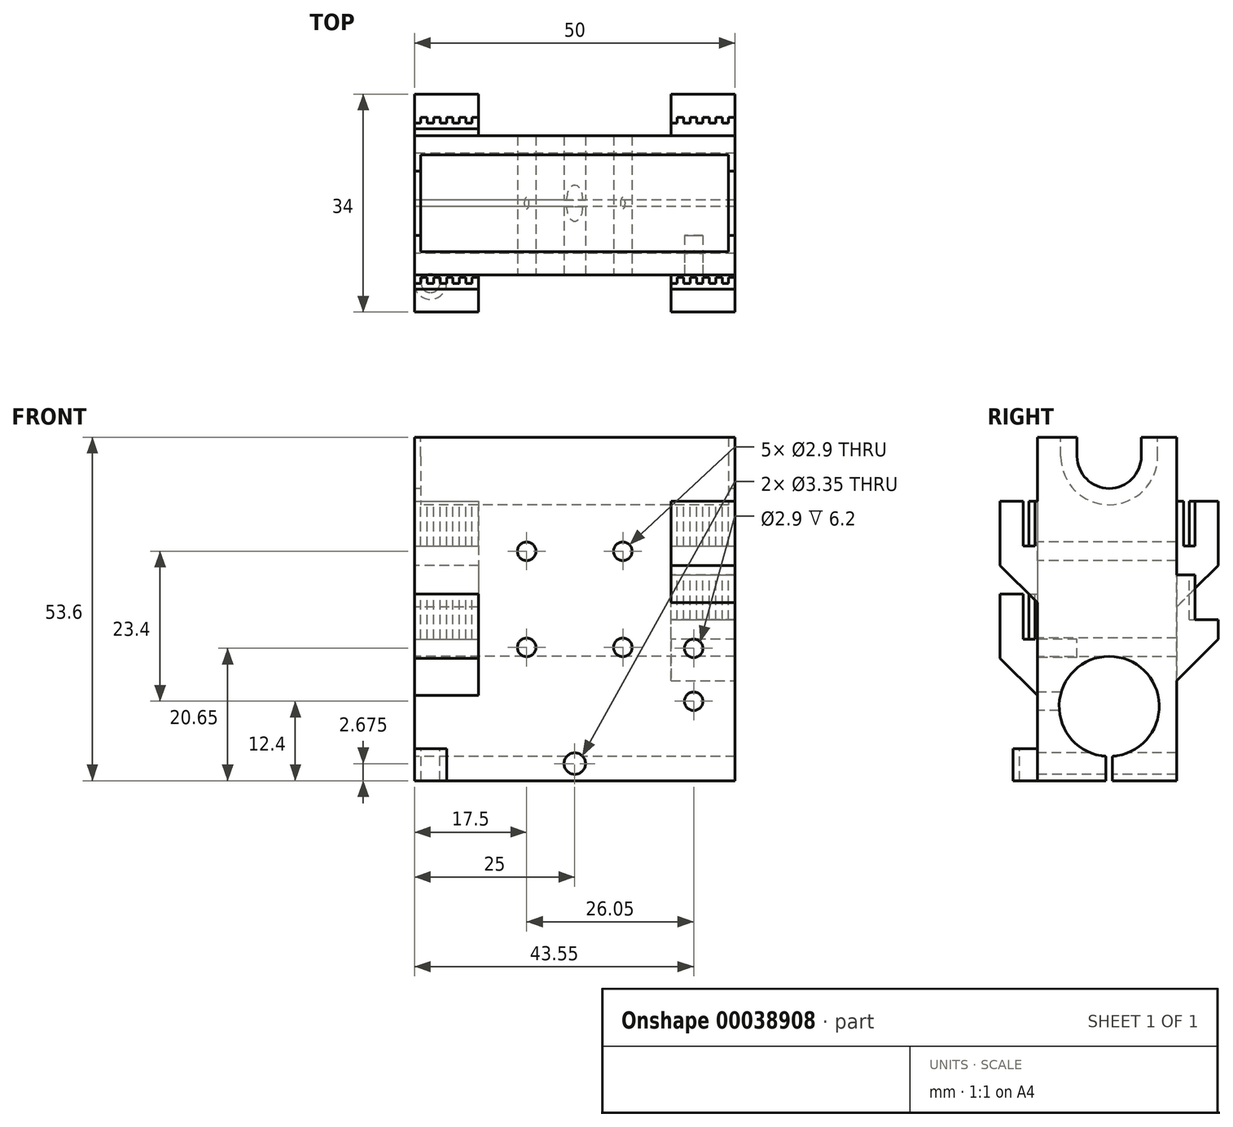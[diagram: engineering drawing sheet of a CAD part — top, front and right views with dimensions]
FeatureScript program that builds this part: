
annotation { "Feature Type Name" : "Feature", "Feature Type Description" : "" }
export const myFeature = defineFeature(function(context is Context, id is Id, definition is map)
    precondition{}
    {
        {
            var Q0;
            Q0=qCreatedBy(makeId("Top.planeOp"),FACE);
            var sketch = newSketch(context, id + "F0", { "sketchPlane" : qUnion([Q0])});
            skLineSegment(sketch, "E0.bottom", {"start": v(0, 0) * mm, "end": v(50, 0) * mm});
            skLineSegment(sketch, "E0.top", {"start": v(0, 20) * mm, "end": v(50, 20) * mm});
            skLineSegment(sketch, "E0.left", {"start": v(0, 0) * mm, "end": v(0, 20) * mm});
            skLineSegment(sketch, "E0.right", {"start": v(50, 0) * mm, "end": v(50, 20) * mm});
            skSolve(sketch);
        }
        {
            var Q0;
            Q0=qSketchRegion(id+"F0",true);
            extrude(context, id + "F1", {"entities" : qUnion([Q0]), "depth" : 50.6 * mm, "hasSecondDirection" : true, "secondDirectionOppositeDirection" : true, "secondDirectionDepth" : 3 * mm});
        }
        {
            var Q0;
            Q0=makeQuery(id+"F1.opExtrude","SWEPT_FACE",FACE,{"disambiguationData":[OSD([sQuery(id+"F0.wireOp",EDGE,"E0.left")])]});
            var sketch = newSketch(context, id + "F2", { "sketchPlane" : qUnion([Q0])});
            skCircle(sketch, "E1", {"center": v(-10, 8.6) * mm, "radius": 7.8 * mm});
            skCircle(sketch, "E2", {"center": v(-10, 47.6) * mm, "radius": 5 * mm});
            skLineSegment(sketch, "E3", {"start": v(-20, 47.6) * mm, "end": v(0, 47.6) * mm, "construction": true});
            skLineSegment(sketch, "E4", {"start": v(-15, 50.6) * mm, "end": v(-15, 47.6) * mm});
            skLineSegment(sketch, "E5", {"start": v(-5, 50.6) * mm, "end": v(-5, 47.6) * mm});
            skLineSegment(sketch, "E6", {"start": v(-20, 8.6) * mm, "end": v(0, 8.6) * mm, "construction": true});
            skLineSegment(sketch, "E7", {"start": v(-10, 8.6) * mm, "end": v(-10, -3) * mm, "construction": true});
            skLineSegment(sketch, "E8", {"start": v(-10, -3) * mm, "end": v(-10.5, -3) * mm});
            skLineSegment(sketch, "E9", {"start": v(-10.5, -3) * mm, "end": v(-10.5, 0.82) * mm});
            skLineSegment(sketch, "E10", {"start": v(-10.5, 0.82) * mm, "end": v(-9.5, 0.82) * mm});
            skLineSegment(sketch, "E11", {"start": v(-9.5, 0.82) * mm, "end": v(-9.5, 0) * mm});
            skLineSegment(sketch, "E12", {"start": v(-9.5, -3) * mm, "end": v(-10, -3) * mm});
            skLineSegment(sketch, "E13", {"start": v(-10, 15.6) * mm, "end": v(-10, 16.4) * mm});
            skLineSegment(sketch, "E14", {"start": v(-10, 15.6) * mm, "end": v(-5.38, 14.88) * mm});
            skLineSegment(sketch, "E15", {"start": v(-10, 15.6) * mm, "end": v(-14.62, 14.88) * mm});
            skCircle(sketch, "E16", {"center": v(-10, 47.6) * mm, "radius": 7.55 * mm});
            skLineSegment(sketch, "E17", {"start": v(-2.45, 47.6) * mm, "end": v(-2.45, 50.6) * mm});
            skLineSegment(sketch, "E18", {"start": v(-17.55, 47.6) * mm, "end": v(-17.55, 50.6) * mm});
            skLineSegment(sketch, "E19", {"start": v(-9.5, -3) * mm, "end": v(-9.5, 0) * mm});
            skSolve(sketch);
        }
        {
            var Q0;
            {var subQ0=sQuery(id+"F2.wireOp",EDGE,"E14");var subQ1=sQuery(id+"F2.wireOp",EDGE,"E1");var subQ3=makeQuery(id+"F2.imprint","INTERSECT",VERTEX,{"disambiguationData":[OD(0.0)],"derivedFrom":[subQ1,subQ0]});Q0=makeQuery(id+"F2.imprint","IMPRINT",FACE,{"disambiguationData":[TD([[makeQuery(id+"F2.imprint","IMPRINT",EDGE,{"disambiguationData":[TD([[subQ3,-1.0]])],"derivedFrom":subQ1}),1.0]])]});}
            var Q1;
            {var subQ0=sQuery(id+"F2.wireOp",EDGE,"E15");var subQ1=sQuery(id+"F2.wireOp",EDGE,"E1");var subQ3=makeQuery(id+"F2.imprint","INTERSECT",VERTEX,{"disambiguationData":[OD(0.0)],"derivedFrom":[subQ1,subQ0]});Q1=makeQuery(id+"F2.imprint","IMPRINT",FACE,{"disambiguationData":[TD([[makeQuery(id+"F2.imprint","IMPRINT",EDGE,{"disambiguationData":[TD([[subQ3,1.0]])],"derivedFrom":subQ1}),1.0]])]});}
            var Q2;
            Q2=makeQuery(id+"F2.imprint","IMPRINT",FACE,{"disambiguationData":[TD([[makeQuery(id+"F2.imprint","IMPRINT",EDGE,{"derivedFrom":sQuery(id+"F2.wireOp",EDGE,"E8")}),-1.0]])]});
            var Q3;
            {var subQ0=sQuery(id+"F2.wireOp",EDGE,"E10");Q3=makeQuery(id+"F2.imprint","IMPRINT",FACE,{"disambiguationData":[TD([[makeQuery(id+"F2.imprint","IMPRINT",EDGE,{"derivedFrom":subQ0}),-1.0]])]});}
            var Q4;
            {var subQ3=sQuery(id+"F2.wireOp",EDGE,"E13");Q4=makeQuery(id+"F2.imprint","IMPRINT",FACE,{"disambiguationData":[TD([[makeQuery(id+"F2.imprint","IMPRINT",EDGE,{"derivedFrom":subQ3}),-1.0]])]});}
            var Q5;
            {var subQ3=sQuery(id+"F2.wireOp",EDGE,"E13");Q5=makeQuery(id+"F2.imprint","IMPRINT",FACE,{"disambiguationData":[TD([[makeQuery(id+"F2.imprint","IMPRINT",EDGE,{"derivedFrom":subQ3}),1.0]])]});}
            var Q6;
            {var subQ7=sQuery(id+"F2.wireOp",EDGE,"E10");Q6=makeQuery(id+"F2.imprint","IMPRINT",FACE,{"disambiguationData":[TD([[makeQuery(id+"F2.imprint","IMPRINT",EDGE,{"derivedFrom":subQ7}),1.0]])]});}
            var Q7;
            {var subQ3=sQuery(id+"F2.wireOp",EDGE,"E5");Q7=makeQuery(id+"F2.imprint","IMPRINT",FACE,{"disambiguationData":[TD([[makeQuery(id+"F2.imprint","IMPRINT",EDGE,{"derivedFrom":subQ3}),-1.0]])]});}
            var Q8;
            {var subQ0=sQuery(id+"F2.wireOp",EDGE,"E4");Q8=makeQuery(id+"F2.imprint","IMPRINT",FACE,{"disambiguationData":[TD([[makeQuery(id+"F2.imprint","IMPRINT",EDGE,{"derivedFrom":subQ0}),1.0]])]});}
            var Q9;
            {var subQ0=sQuery(id+"F2.wireOp",EDGE,"E4");Q9=makeQuery(id+"F2.imprint","IMPRINT",FACE,{"disambiguationData":[TD([[makeQuery(id+"F2.imprint","IMPRINT",EDGE,{"derivedFrom":subQ0}),1.0]])]});}
            var Q10;
            {var subQ3=sQuery(id+"F2.wireOp",EDGE,"E5");Q10=makeQuery(id+"F2.imprint","IMPRINT",FACE,{"disambiguationData":[TD([[makeQuery(id+"F2.imprint","IMPRINT",EDGE,{"derivedFrom":subQ3}),-1.0]])]});}
            var Q11;
            {var subQ1=sQuery(id+"F2.wireOp",EDGE,"E2");var subQ4=makeQuery(id+"F2.imprint","INTERSECT",VERTEX,{"derivedFrom":[subQ1,sQuery(id+"F2.wireOp",EDGE,"E5")]});Q11=makeQuery(id+"F2.imprint","IMPRINT",FACE,{"disambiguationData":[TD([[makeQuery(id+"F2.imprint","IMPRINT",EDGE,{"disambiguationData":[TD([[subQ4,-1.0]])],"derivedFrom":subQ1}),1.0]])]});}
            extrude(context, id + "F3", {"entities" : qUnion([Q0, Q1, Q2, Q3, Q4, Q5, Q6, Q7, Q8, Q9, Q10, Q11]), "operationType" : NewBodyOperationType.REMOVE, "endBound" : BoundingType.THROUGH_ALL, "oppositeDirection" : true, "depth" : 25 * mm});
        }
        {
            var Q0;
            {var subQ3=sQuery(id+"F2.wireOp",EDGE,"E4");Q0=makeQuery(id+"F2.imprint","IMPRINT",FACE,{"disambiguationData":[TD([[makeQuery(id+"F2.imprint","IMPRINT",EDGE,{"derivedFrom":subQ3}),-1.0]])]});}
            var Q1;
            {var subQ3=sQuery(id+"F2.wireOp",EDGE,"E18");Q1=makeQuery(id+"F2.imprint","IMPRINT",FACE,{"disambiguationData":[TD([[makeQuery(id+"F2.imprint","IMPRINT",EDGE,{"derivedFrom":subQ3}),-1.0]])]});}
            var Q2;
            {var subQ3=sQuery(id+"F2.wireOp",EDGE,"E17");Q2=makeQuery(id+"F2.imprint","IMPRINT",FACE,{"disambiguationData":[TD([[makeQuery(id+"F2.imprint","IMPRINT",EDGE,{"derivedFrom":subQ3}),1.0]])]});}
            extrude(context, id + "F4", {"entities" : qUnion([Q0, Q1, Q2]), "operationType" : NewBodyOperationType.REMOVE, "oppositeDirection" : true, "depth" : 49 * mm});
        }
        {
            var Q0;
            {var subQ3=sQuery(id+"F2.wireOp",EDGE,"E4");Q0=makeQuery(id+"F2.imprint","IMPRINT",FACE,{"disambiguationData":[TD([[makeQuery(id+"F2.imprint","IMPRINT",EDGE,{"derivedFrom":subQ3}),-1.0]])]});}
            var Q1;
            {var subQ3=sQuery(id+"F2.wireOp",EDGE,"E18");Q1=makeQuery(id+"F2.imprint","IMPRINT",FACE,{"disambiguationData":[TD([[makeQuery(id+"F2.imprint","IMPRINT",EDGE,{"derivedFrom":subQ3}),-1.0]])]});}
            var Q2;
            {var subQ3=sQuery(id+"F2.wireOp",EDGE,"E17");Q2=makeQuery(id+"F2.imprint","IMPRINT",FACE,{"disambiguationData":[TD([[makeQuery(id+"F2.imprint","IMPRINT",EDGE,{"derivedFrom":subQ3}),1.0]])]});}
            extrude(context, id + "F5", {"entities" : qUnion([Q0, Q1, Q2]), "operationType" : NewBodyOperationType.ADD, "oppositeDirection" : true, "depth" : 16.21 * mm});
        }
        {
            var Q0;
            {var subQ3=sQuery(id+"F2.wireOp",EDGE,"E4");Q0=makeQuery(id+"F2.imprint","IMPRINT",FACE,{"disambiguationData":[TD([[makeQuery(id+"F2.imprint","IMPRINT",EDGE,{"derivedFrom":subQ3}),-1.0]])]});}
            var Q1;
            {var subQ3=sQuery(id+"F2.wireOp",EDGE,"E18");Q1=makeQuery(id+"F2.imprint","IMPRINT",FACE,{"disambiguationData":[TD([[makeQuery(id+"F2.imprint","IMPRINT",EDGE,{"derivedFrom":subQ3}),-1.0]])]});}
            var Q2;
            {var subQ3=sQuery(id+"F2.wireOp",EDGE,"E17");Q2=makeQuery(id+"F2.imprint","IMPRINT",FACE,{"disambiguationData":[TD([[makeQuery(id+"F2.imprint","IMPRINT",EDGE,{"derivedFrom":subQ3}),1.0]])]});}
            extrude(context, id + "F6", {"entities" : qUnion([Q0, Q1, Q2]), "operationType" : NewBodyOperationType.REMOVE, "oppositeDirection" : true, "depth" : 23.25 * mm});
        }
        {
            var Q0;
            {var subQ3=sQuery(id+"F2.wireOp",EDGE,"E4");Q0=makeQuery(id+"F2.imprint","IMPRINT",FACE,{"disambiguationData":[TD([[makeQuery(id+"F2.imprint","IMPRINT",EDGE,{"derivedFrom":subQ3}),-1.0]])]});}
            var Q1;
            {var subQ3=sQuery(id+"F2.wireOp",EDGE,"E18");Q1=makeQuery(id+"F2.imprint","IMPRINT",FACE,{"disambiguationData":[TD([[makeQuery(id+"F2.imprint","IMPRINT",EDGE,{"derivedFrom":subQ3}),-1.0]])]});}
            var Q2;
            {var subQ3=sQuery(id+"F2.wireOp",EDGE,"E17");Q2=makeQuery(id+"F2.imprint","IMPRINT",FACE,{"disambiguationData":[TD([[makeQuery(id+"F2.imprint","IMPRINT",EDGE,{"derivedFrom":subQ3}),1.0]])]});}
            extrude(context, id + "F7", {"entities" : qUnion([Q0, Q1, Q2]), "operationType" : NewBodyOperationType.ADD, "oppositeDirection" : true, "depth" : 1 * mm});
        }
        {
            var Q0;
            Q0=makeQuery(id+"F1.opExtrude","SWEPT_FACE",FACE,{"disambiguationData":[OSD([sQuery(id+"F0.wireOp",EDGE,"E0.bottom")])]});
            var sketch = newSketch(context, id + "F8", { "sketchPlane" : qUnion([Q0])});
            skLineSegment(sketch, "E20.bottom", {"start": v(0, 26.1) * mm, "end": v(10, 26.1) * mm});
            skLineSegment(sketch, "E20.top", {"start": v(0, 6.1) * mm, "end": v(10, 6.1) * mm});
            skLineSegment(sketch, "E20.left", {"start": v(0, 26.1) * mm, "end": v(0, 6.1) * mm});
            skLineSegment(sketch, "E20.right", {"start": v(10, 26.1) * mm, "end": v(10, 6.1) * mm});
            skLineSegment(sketch, "E21.bottom", {"start": v(50, 40.6) * mm, "end": v(40, 40.6) * mm});
            skLineSegment(sketch, "E21.top", {"start": v(50, 20.6) * mm, "end": v(40, 20.6) * mm});
            skLineSegment(sketch, "E21.left", {"start": v(50, 40.6) * mm, "end": v(50, 20.6) * mm});
            skLineSegment(sketch, "E21.right", {"start": v(40, 40.6) * mm, "end": v(40, 20.6) * mm});
            skPoint(sketch, "E22", {"position": v(0, 47.6) * mm});
            skPoint(sketch, "E23", {"position": v(0, 5.6) * mm});
            skSolve(sketch);
        }
        {
            var Q0;
            Q0=qSketchRegion(id+"F8",true);
            extrude(context, id + "F9", {"entities" : qUnion([Q0]), "operationType" : NewBodyOperationType.ADD, "depth" : 7 * mm});
        }
        {
            var Q0;
            Q0=makeQuery(id+"F9.opExtrude","SWEPT_FACE",FACE,{"disambiguationData":[OSD([sQuery(id+"F8.wireOp",EDGE,"E20.bottom")])]});
            var sketch = newSketch(context, id + "F10", { "sketchPlane" : qUnion([Q0])});
            skLineSegment(sketch, "E24", {"start": v(-935.9, 0) * mm, "end": v(-935.88, -4.54) * mm});
            skLineSegment(sketch, "E25.left", {"start": v(0, -3.4) * mm, "end": v(0, -1.6) * mm});
            skLineSegment(sketch, "E26", {"start": v(6, -2.5) * mm, "end": v(7, -2.5) * mm});
            skLineSegment(sketch, "E27", {"start": v(4, -2.5) * mm, "end": v(5, -2.5) * mm});
            skLineSegment(sketch, "E28", {"start": v(0, -2.5) * mm, "end": v(1, -2.5) * mm});
            skLineSegment(sketch, "E29", {"start": v(7, -1.6) * mm, "end": v(8, -1.6) * mm});
            skLineSegment(sketch, "E30", {"start": v(2, -2.5) * mm, "end": v(3, -2.5) * mm});
            skLineSegment(sketch, "E31", {"start": v(3, -1.6) * mm, "end": v(4, -1.6) * mm});
            skLineSegment(sketch, "E32", {"start": v(8, -2.5) * mm, "end": v(9, -2.5) * mm});
            skLineSegment(sketch, "E33", {"start": v(8, -1.6) * mm, "end": v(8, -2.5) * mm});
            skLineSegment(sketch, "E34", {"start": v(9, -2.5) * mm, "end": v(9, -1.6) * mm});
            skLineSegment(sketch, "E35", {"start": v(10, -1.6) * mm, "end": v(10, -2.5) * mm});
            skLineSegment(sketch, "E36", {"start": v(6, -1.6) * mm, "end": v(6, -2.5) * mm});
            skLineSegment(sketch, "E37", {"start": v(2, -1.6) * mm, "end": v(2, -2.5) * mm});
            skLineSegment(sketch, "E38", {"start": v(1, -1.6) * mm, "end": v(2, -1.6) * mm});
            skLineSegment(sketch, "E39", {"start": v(1, -2.5) * mm, "end": v(1, -1.6) * mm});
            skLineSegment(sketch, "E40", {"start": v(9, -1.6) * mm, "end": v(10, -1.6) * mm});
            skLineSegment(sketch, "E41", {"start": v(5, -1.6) * mm, "end": v(6, -1.6) * mm});
            skLineSegment(sketch, "E42", {"start": v(5, -2.5) * mm, "end": v(5, -1.6) * mm});
            skLineSegment(sketch, "E43", {"start": v(3, -2.5) * mm, "end": v(3, -1.6) * mm});
            skLineSegment(sketch, "E44", {"start": v(4, -1.6) * mm, "end": v(4, -2.5) * mm});
            skLineSegment(sketch, "E45", {"start": v(7, -2.5) * mm, "end": v(7, -1.6) * mm});
            skLineSegment(sketch, "E46", {"start": v(0, -1.6) * mm, "end": v(0, -2.5) * mm});
            skLineSegment(sketch, "E47", {"start": v(10, -2.5) * mm, "end": v(10, -3.4) * mm});
            skLineSegment(sketch, "E48", {"start": v(0, -3.4) * mm, "end": v(10, -3.4) * mm});
            skLineSegment(sketch, "E49", {"start": v(5.3, -1.6) * mm, "end": v(5.3, 0) * mm});
            skSolve(sketch);
        }
        {
            var Q0;
            Q0=qSketchRegion(id+"F10",true);
            extrude(context, id + "F11", {"entities" : qUnion([Q0]), "operationType" : NewBodyOperationType.REMOVE, "oppositeDirection" : true, "depth" : 7 * mm});
        }
        {
            var Q0;
            Q0=makeQuery(id+"F9.opExtrude","SWEPT_FACE",FACE,{"disambiguationData":[OSD([sQuery(id+"F8.wireOp",EDGE,"E21.bottom")])]});
            var sketch = newSketch(context, id + "F12", { "sketchPlane" : qUnion([Q0])});
            skLineSegment(sketch, "E50.left", {"start": v(40, -3.4) * mm, "end": v(40, -1.6) * mm});
            skLineSegment(sketch, "E51", {"start": v(46, -2.5) * mm, "end": v(47, -2.5) * mm});
            skLineSegment(sketch, "E52", {"start": v(44, -2.5) * mm, "end": v(45, -2.5) * mm});
            skLineSegment(sketch, "E53", {"start": v(40, -2.5) * mm, "end": v(41, -2.5) * mm});
            skLineSegment(sketch, "E54", {"start": v(47, -1.6) * mm, "end": v(48, -1.6) * mm});
            skLineSegment(sketch, "E55", {"start": v(42, -2.5) * mm, "end": v(43, -2.5) * mm});
            skLineSegment(sketch, "E56", {"start": v(43, -1.6) * mm, "end": v(44, -1.6) * mm});
            skLineSegment(sketch, "E57", {"start": v(48, -2.5) * mm, "end": v(49, -2.5) * mm});
            skLineSegment(sketch, "E58", {"start": v(48, -1.6) * mm, "end": v(48, -2.5) * mm});
            skLineSegment(sketch, "E59", {"start": v(49, -2.5) * mm, "end": v(49, -1.6) * mm});
            skLineSegment(sketch, "E60", {"start": v(50, -1.6) * mm, "end": v(50, -2.5) * mm});
            skLineSegment(sketch, "E61", {"start": v(46, -1.6) * mm, "end": v(46, -2.5) * mm});
            skLineSegment(sketch, "E62", {"start": v(42, -1.6) * mm, "end": v(42, -2.5) * mm});
            skLineSegment(sketch, "E63", {"start": v(41, -1.6) * mm, "end": v(42, -1.6) * mm});
            skLineSegment(sketch, "E64", {"start": v(41, -2.5) * mm, "end": v(41, -1.6) * mm});
            skLineSegment(sketch, "E65", {"start": v(49, -1.6) * mm, "end": v(50, -1.6) * mm});
            skLineSegment(sketch, "E66", {"start": v(45, -1.6) * mm, "end": v(46, -1.6) * mm});
            skLineSegment(sketch, "E67", {"start": v(45, -2.5) * mm, "end": v(45, -1.6) * mm});
            skLineSegment(sketch, "E68", {"start": v(43, -2.5) * mm, "end": v(43, -1.6) * mm});
            skLineSegment(sketch, "E69", {"start": v(44, -1.6) * mm, "end": v(44, -2.5) * mm});
            skLineSegment(sketch, "E70", {"start": v(47, -2.5) * mm, "end": v(47, -1.6) * mm});
            skLineSegment(sketch, "E71", {"start": v(40, -1.6) * mm, "end": v(40, -2.5) * mm});
            skLineSegment(sketch, "E72", {"start": v(50, -2.5) * mm, "end": v(50, -3.4) * mm});
            skLineSegment(sketch, "E73", {"start": v(40, -3.4) * mm, "end": v(50, -3.4) * mm});
            skLineSegment(sketch, "E74", {"start": v(45.23, -1.6) * mm, "end": v(45.23, 0) * mm});
            skSolve(sketch);
        }
        {
            var Q0;
            Q0=qSketchRegion(id+"F12",true);
            extrude(context, id + "F13", {"entities" : qUnion([Q0]), "operationType" : NewBodyOperationType.REMOVE, "oppositeDirection" : true, "depth" : 7 * mm});
        }
        {
            var Q0;
            Q0=makeQuery(id+"F1.opExtrude","SWEPT_FACE",FACE,{"disambiguationData":[OSD([sQuery(id+"F0.wireOp",EDGE,"E0.top")])]});
            var sketch = newSketch(context, id + "F14", { "sketchPlane" : qUnion([Q0])});
            skLineSegment(sketch, "E75.bottom", {"start": v(-50, 9.1) * mm, "end": v(-40, 9.1) * mm});
            skLineSegment(sketch, "E75.top", {"start": v(-50, 29.1) * mm, "end": v(-40, 29.1) * mm});
            skLineSegment(sketch, "E75.left", {"start": v(-50, 9.1) * mm, "end": v(-50, 29.1) * mm});
            skLineSegment(sketch, "E75.right", {"start": v(-40, 9.1) * mm, "end": v(-40, 29.1) * mm});
            skLineSegment(sketch, "E76.bottom", {"start": v(0, 40.6) * mm, "end": v(-10, 40.6) * mm});
            skLineSegment(sketch, "E76.top", {"start": v(0, 20.6) * mm, "end": v(-10, 20.6) * mm});
            skLineSegment(sketch, "E76.left", {"start": v(0, 40.6) * mm, "end": v(0, 20.6) * mm});
            skLineSegment(sketch, "E76.right", {"start": v(-10, 40.6) * mm, "end": v(-10, 20.6) * mm});
            skSolve(sketch);
        }
        {
            var Q0;
            Q0=qSketchRegion(id+"F14",true);
            extrude(context, id + "F15", {"entities" : qUnion([Q0]), "operationType" : NewBodyOperationType.ADD, "depth" : 7 * mm});
        }
        {
            var Q0;
            Q0=makeQuery(id+"F15.opExtrude","SWEPT_FACE",FACE,{"disambiguationData":[OSD([sQuery(id+"F14.wireOp",EDGE,"E75.top")])]});
            var sketch = newSketch(context, id + "F16", { "sketchPlane" : qUnion([Q0])});
            skLineSegment(sketch, "E77.left", {"start": v(40, 21.6) * mm, "end": v(40, 23.4) * mm});
            skLineSegment(sketch, "E78", {"start": v(46, 22.5) * mm, "end": v(47, 22.5) * mm});
            skLineSegment(sketch, "E79", {"start": v(44, 22.5) * mm, "end": v(45, 22.5) * mm});
            skLineSegment(sketch, "E80", {"start": v(40, 22.5) * mm, "end": v(41, 22.5) * mm});
            skLineSegment(sketch, "E81", {"start": v(47, 23.4) * mm, "end": v(48, 23.4) * mm});
            skLineSegment(sketch, "E82", {"start": v(42, 22.5) * mm, "end": v(43, 22.5) * mm});
            skLineSegment(sketch, "E83", {"start": v(43, 23.4) * mm, "end": v(44, 23.4) * mm});
            skLineSegment(sketch, "E84", {"start": v(48, 22.5) * mm, "end": v(49, 22.5) * mm});
            skLineSegment(sketch, "E85", {"start": v(48, 23.4) * mm, "end": v(48, 22.5) * mm});
            skLineSegment(sketch, "E86", {"start": v(49, 22.5) * mm, "end": v(49, 23.4) * mm});
            skLineSegment(sketch, "E87", {"start": v(50, 23.4) * mm, "end": v(50, 22.5) * mm});
            skLineSegment(sketch, "E88", {"start": v(46, 23.4) * mm, "end": v(46, 22.5) * mm});
            skLineSegment(sketch, "E89", {"start": v(42, 23.4) * mm, "end": v(42, 22.5) * mm});
            skLineSegment(sketch, "E90", {"start": v(41, 23.4) * mm, "end": v(42, 23.4) * mm});
            skLineSegment(sketch, "E91", {"start": v(41, 22.5) * mm, "end": v(41, 23.4) * mm});
            skLineSegment(sketch, "E92", {"start": v(49, 23.4) * mm, "end": v(50, 23.4) * mm});
            skLineSegment(sketch, "E93", {"start": v(45, 23.4) * mm, "end": v(46, 23.4) * mm});
            skLineSegment(sketch, "E94", {"start": v(45, 22.5) * mm, "end": v(45, 23.4) * mm});
            skLineSegment(sketch, "E95", {"start": v(43, 22.5) * mm, "end": v(43, 23.4) * mm});
            skLineSegment(sketch, "E96", {"start": v(44, 23.4) * mm, "end": v(44, 22.5) * mm});
            skLineSegment(sketch, "E97", {"start": v(47, 22.5) * mm, "end": v(47, 23.4) * mm});
            skLineSegment(sketch, "E98", {"start": v(40, 23.4) * mm, "end": v(40, 22.5) * mm});
            skLineSegment(sketch, "E99", {"start": v(50, 22.5) * mm, "end": v(50, 21.6) * mm});
            skLineSegment(sketch, "E100", {"start": v(40, 21.6) * mm, "end": v(50, 21.6) * mm});
            skLineSegment(sketch, "E101", {"start": v(45, 21.6) * mm, "end": v(45, 20) * mm});
            skSolve(sketch);
        }
        {
            var Q0;
            {var subQ4=sQuery(id+"F16.wireOp",EDGE,"E77.left");Q0=makeQuery(id+"F16.imprint","IMPRINT",FACE,{"disambiguationData":[TD([[makeQuery(id+"F16.imprint","IMPRINT",EDGE,{"derivedFrom":subQ4}),1.0]])]});}
            extrude(context, id + "F17", {"entities" : qUnion([Q0]), "operationType" : NewBodyOperationType.REMOVE, "oppositeDirection" : true, "depth" : 7 * mm});
        }
        {
            var Q0;
            Q0=makeQuery(id+"F15.opExtrude","SWEPT_FACE",FACE,{"disambiguationData":[OSD([sQuery(id+"F14.wireOp",EDGE,"E76.bottom")])]});
            var sketch = newSketch(context, id + "F18", { "sketchPlane" : qUnion([Q0])});
            skLineSegment(sketch, "E102", {"start": v(6, 22.5) * mm, "end": v(7, 22.5) * mm});
            skLineSegment(sketch, "E103", {"start": v(4, 22.5) * mm, "end": v(5, 22.5) * mm});
            skLineSegment(sketch, "E104", {"start": v(0, 22.5) * mm, "end": v(1, 22.5) * mm});
            skLineSegment(sketch, "E105", {"start": v(7, 23.4) * mm, "end": v(8, 23.4) * mm});
            skLineSegment(sketch, "E106", {"start": v(2, 22.5) * mm, "end": v(3, 22.5) * mm});
            skLineSegment(sketch, "E107", {"start": v(3, 23.4) * mm, "end": v(4, 23.4) * mm});
            skLineSegment(sketch, "E108", {"start": v(8, 22.5) * mm, "end": v(9, 22.5) * mm});
            skLineSegment(sketch, "E109", {"start": v(8, 23.4) * mm, "end": v(8, 22.5) * mm});
            skLineSegment(sketch, "E110", {"start": v(9, 22.5) * mm, "end": v(9, 23.4) * mm});
            skLineSegment(sketch, "E111", {"start": v(10, 23.4) * mm, "end": v(10, 22.5) * mm});
            skLineSegment(sketch, "E112", {"start": v(6, 23.4) * mm, "end": v(6, 22.5) * mm});
            skLineSegment(sketch, "E113", {"start": v(2, 23.4) * mm, "end": v(2, 22.5) * mm});
            skLineSegment(sketch, "E114", {"start": v(1, 23.4) * mm, "end": v(2, 23.4) * mm});
            skLineSegment(sketch, "E115", {"start": v(1, 22.5) * mm, "end": v(1, 23.4) * mm});
            skLineSegment(sketch, "E116", {"start": v(9, 23.4) * mm, "end": v(10, 23.4) * mm});
            skLineSegment(sketch, "E117", {"start": v(5, 23.4) * mm, "end": v(6, 23.4) * mm});
            skLineSegment(sketch, "E118", {"start": v(5, 22.5) * mm, "end": v(5, 23.4) * mm});
            skLineSegment(sketch, "E119", {"start": v(3, 22.5) * mm, "end": v(3, 23.4) * mm});
            skLineSegment(sketch, "E120", {"start": v(4, 23.4) * mm, "end": v(4, 22.5) * mm});
            skLineSegment(sketch, "E121", {"start": v(7, 22.5) * mm, "end": v(7, 23.4) * mm});
            skLineSegment(sketch, "E122", {"start": v(10, 22.5) * mm, "end": v(10, 21.6) * mm});
            skLineSegment(sketch, "E123", {"start": v(0, 21.6) * mm, "end": v(10, 21.6) * mm});
            skLineSegment(sketch, "E124", {"start": v(5, 21.6) * mm, "end": v(5, 20) * mm});
            skLineSegment(sketch, "E125", {"start": v(0, 21.6) * mm, "end": v(0, 22.5) * mm});
            skSolve(sketch);
        }
        {
            var Q0;
            Q0=makeQuery(id+"F18.imprint","IMPRINT",FACE,{"disambiguationData":[TD([[makeQuery(id+"F18.imprint","IMPRINT",EDGE,{"derivedFrom":sQuery(id+"F18.wireOp",EDGE,"E102")}),-1.0]])]});
            extrude(context, id + "F19", {"entities" : qUnion([Q0]), "operationType" : NewBodyOperationType.REMOVE, "oppositeDirection" : true, "depth" : 7 * mm});
        }
        {
            var Q0;
            Q0=makeQuery(id+"F1.opExtrude","SWEPT_FACE",FACE,{"disambiguationData":[OSD([sQuery(id+"F0.wireOp",EDGE,"E0.bottom")])]});
            var sketch = newSketch(context, id + "F20", { "sketchPlane" : qUnion([Q0])});
            skCircle(sketch, "E126", {"center": v(17.5, 32.8) * mm, "radius": 1.45 * mm});
            skCircle(sketch, "E127", {"center": v(32.5, 32.8) * mm, "radius": 1.45 * mm});
            skCircle(sketch, "E128", {"center": v(17.5, 17.8) * mm, "radius": 1.45 * mm});
            skCircle(sketch, "E129", {"center": v(32.5, 17.8) * mm, "radius": 1.45 * mm});
            skLineSegment(sketch, "E130", {"start": v(17.5, 32.8) * mm, "end": v(0, 32.8) * mm});
            skLineSegment(sketch, "E131", {"start": v(32.5, 17.8) * mm, "end": v(50, 17.8) * mm});
            skLineSegment(sketch, "E132", {"start": v(32.5, 32.8) * mm, "end": v(32.5, 50.6) * mm});
            skLineSegment(sketch, "E133", {"start": v(17.5, 17.8) * mm, "end": v(17.5, 0) * mm});
            skCircle(sketch, "E134", {"center": v(25, -0.32) * mm, "radius": 1.68 * mm});
            skLineSegment(sketch, "E135", {"start": v(25, -3) * mm, "end": v(25, 13.82) * mm, "construction": true});
            skSolve(sketch);
        }
        {
            var Q0;
            Q0=qSketchRegion(id+"F20",true);
            var Q1;
            Q1=makeQuery(id+"F20.imprint","IMPRINT",FACE,{"disambiguationData":[TD([[makeQuery(id+"F20.imprint","IMPRINT",EDGE,{"derivedFrom":sQuery(id+"F20.wireOp",EDGE,"E126")}),1.0]])]});
            var Q2;
            Q2=makeQuery(id+"F20.imprint","IMPRINT",FACE,{"disambiguationData":[TD([[makeQuery(id+"F20.imprint","IMPRINT",EDGE,{"derivedFrom":sQuery(id+"F20.wireOp",EDGE,"E127")}),1.0]])]});
            var Q3;
            Q3=makeQuery(id+"F20.imprint","IMPRINT",FACE,{"disambiguationData":[TD([[makeQuery(id+"F20.imprint","IMPRINT",EDGE,{"derivedFrom":sQuery(id+"F20.wireOp",EDGE,"E129")}),1.0]])]});
            var Q4;
            Q4=makeQuery(id+"F20.imprint","IMPRINT",FACE,{"disambiguationData":[TD([[makeQuery(id+"F20.imprint","IMPRINT",EDGE,{"derivedFrom":sQuery(id+"F20.wireOp",EDGE,"E128")}),1.0]])]});
            extrude(context, id + "F21", {"entities" : qUnion([Q0, Q1, Q2, Q3, Q4]), "operationType" : NewBodyOperationType.REMOVE, "endBound" : BoundingType.THROUGH_ALL, "oppositeDirection" : true, "depth" : 25 * mm});
        }
        {
            var Q0;
            Q0=makeQuery(id+"F1.opExtrude","SWEPT_FACE",FACE,{"disambiguationData":[OSD([sQuery(id+"F0.wireOp",EDGE,"E0.bottom")])]});
            var sketch = newSketch(context, id + "F22", { "sketchPlane" : qUnion([Q0])});
            skCircle(sketch, "E136", {"center": v(43.55, 17.65) * mm, "radius": 1.45 * mm});
            skCircle(sketch, "E137", {"center": v(43.55, 9.4) * mm, "radius": 1.45 * mm});
            skSolve(sketch);
        }
        {
            var Q0;
            Q0=qSketchRegion(id+"F22",true);
            extrude(context, id + "F23", {"entities" : qUnion([Q0]), "operationType" : NewBodyOperationType.REMOVE, "oppositeDirection" : true, "depth" : 5 * mm});
        }
        {
            var Q0;
            Q0=makeQuery(id+"F1.opExtrude","SWEPT_FACE",FACE,{"disambiguationData":[OSD([sQuery(id+"F0.wireOp",EDGE,"E0.bottom")])]});
            var sketch = newSketch(context, id + "F24", { "sketchPlane" : qUnion([Q0])});
            skLineSegment(sketch, "E138.bottom", {"start": v(0, -3) * mm, "end": v(5, -3) * mm});
            skLineSegment(sketch, "E138.top", {"start": v(0, 2) * mm, "end": v(5, 2) * mm});
            skLineSegment(sketch, "E138.left", {"start": v(0, -3) * mm, "end": v(0, 2) * mm});
            skLineSegment(sketch, "E138.right", {"start": v(5, -3) * mm, "end": v(5, 2) * mm});
            skSolve(sketch);
        }
        {
            var Q0;
            Q0=qSketchRegion(id+"F24",true);
            extrude(context, id + "F25", {"entities" : qUnion([Q0]), "operationType" : NewBodyOperationType.ADD, "depth" : 5 * mm});
        }
        {
            var Q0;
            Q0=makeQuery(id+"F25.opExtrude","SWEPT_FACE",FACE,{"disambiguationData":[OSD([sQuery(id+"F24.wireOp",EDGE,"E138.top")])]});
            var sketch = newSketch(context, id + "F26", { "sketchPlane" : qUnion([Q0])});
            skCircle(sketch, "E139", {"center": v(2.5, -2.5) * mm, "radius": 1.45 * mm});
            skLineSegment(sketch, "E140", {"start": v(0, -2.5) * mm, "end": v(5, -2.5) * mm});
            skSolve(sketch);
        }
        {
            var Q0;
            Q0=qSketchRegion(id+"F26",true);
            extrude(context, id + "F27", {"entities" : qUnion([Q0]), "operationType" : NewBodyOperationType.REMOVE, "oppositeDirection" : true, "depth" : 25 * mm});
        }
        {
            var Q0;
            Q0=makeQuery(id+"F25.opExtrude","CAP_EDGE",EDGE,{"disambiguationData":[OSD([sQuery(id+"F24.wireOp",EDGE,"E138.left")])],"isStart":false});
            var Q1;
            Q1=makeQuery(id+"F25.opExtrude","CAP_EDGE",EDGE,{"disambiguationData":[OSD([sQuery(id+"F24.wireOp",EDGE,"E138.right")])],"isStart":false});
            fillet(context, id + "F28", {"entities" : qUnion([Q0, Q1]), "radius" : 2.5 * mm, "tangentPropagation" : true, "allowEdgeOverflow" : false});
        }
        {
            var Q0;
            Q0=makeQuery(id+"F1.opExtrude","SWEPT_FACE",FACE,{"disambiguationData":[OSD([sQuery(id+"F0.wireOp",EDGE,"E0.top")])]});
            var sketch = newSketch(context, id + "F29", { "sketchPlane" : qUnion([Q0])});
            skSolve(sketch);
        }
        {
            var Q0;
            Q0 = qSketchRegion(id + "F29", true);
            var Q1;
            {var subQ0=sQuery(id+"F0.wireOp",EDGE,"E0.top");Q1=makeQuery(id+"F29.imprint","IMPRINT",FACE,{"disambiguationData":[TD([[makeQuery(id+"F29.imprint","IMPRINT",EDGE,{"derivedFrom":makeQuery(id+"F1.opExtrude","CAP_EDGE",EDGE,{"disambiguationData":[OSD([subQ0])],"isStart":true})}),-1.0]])]});}
            var Q2;
            Q2=makeQuery(id+"F17.boolean.opBoolean","COPY",FACE,{"derivedFrom":makeQuery(id+"F17.opExtrude","SWEPT_FACE",FACE,{"disambiguationData":[OSD([sQuery(id+"F16.wireOp",EDGE,"E100")])]})});
            var Q3;
            Q3=makeQuery(id+"F1.opExtrude","SWEPT_BODY",BODY,{"disambiguationData":[OSD([sQuery(id+"F0.wireOp",EDGE,"E0.bottom"),sQuery(id+"F0.wireOp",EDGE,"E0.top"),sQuery(id+"F0.wireOp",EDGE,"E0.left"),sQuery(id+"F0.wireOp",EDGE,"E0.right")])]});
            extrude(context, id + "F30", {"entities" : qUnion([Q0, Q1]), "operationType" : NewBodyOperationType.ADD, "endBoundEntityFace" : qUnion([Q2]), "endBoundEntityBody" : qUnion([Q3]), "depth" : .5 * mm});
        }
        {
            var Q0;
            Q0=makeQuery(id+"F1.opExtrude","SWEPT_FACE",FACE,{"disambiguationData":[OSD([sQuery(id+"F0.wireOp",EDGE,"E0.bottom")])]});
            var Q1;
            Q1=makeQuery(id+"F13.boolean.opBoolean","COPY",FACE,{"derivedFrom":makeQuery(id+"F13.opExtrude","SWEPT_FACE",FACE,{"disambiguationData":[OSD([sQuery(id+"F12.wireOp",EDGE,"E65")])]})});
            extrude(context, id + "F31", {"entities" : qUnion([Q0]), "operationType" : NewBodyOperationType.ADD, "endBoundEntityFace" : qUnion([Q1]), "depth" : 1.2 * mm});
        }
        {
            var Q0;
            Q0=makeQuery(id+"F9.opExtrude","CAP_EDGE",EDGE,{"disambiguationData":[OSD([sQuery(id+"F8.wireOp",EDGE,"E20.top")])],"isStart":false});
            var Q1;
            Q1=makeQuery(id+"F9.opExtrude","CAP_EDGE",EDGE,{"disambiguationData":[OSD([sQuery(id+"F8.wireOp",EDGE,"E21.top")])],"isStart":false});
            chamfer(context, id + "F32", {"entities" : qUnion([Q0, Q1]), "width" : 10 * mm, "tangentPropagation" : true});
        }
        {
            var Q0;
            Q0=makeQuery(id+"F15.opExtrude","CAP_EDGE",EDGE,{"disambiguationData":[OSD([sQuery(id+"F14.wireOp",EDGE,"E75.bottom")])],"isStart":false});
            var Q1;
            Q1=makeQuery(id+"F15.opExtrude","CAP_EDGE",EDGE,{"disambiguationData":[OSD([sQuery(id+"F14.wireOp",EDGE,"E76.top")])],"isStart":false});
            chamfer(context, id + "F33", {"entities" : qUnion([Q0, Q1]), "width" : 10 * mm, "tangentPropagation" : true});
        }
    });
